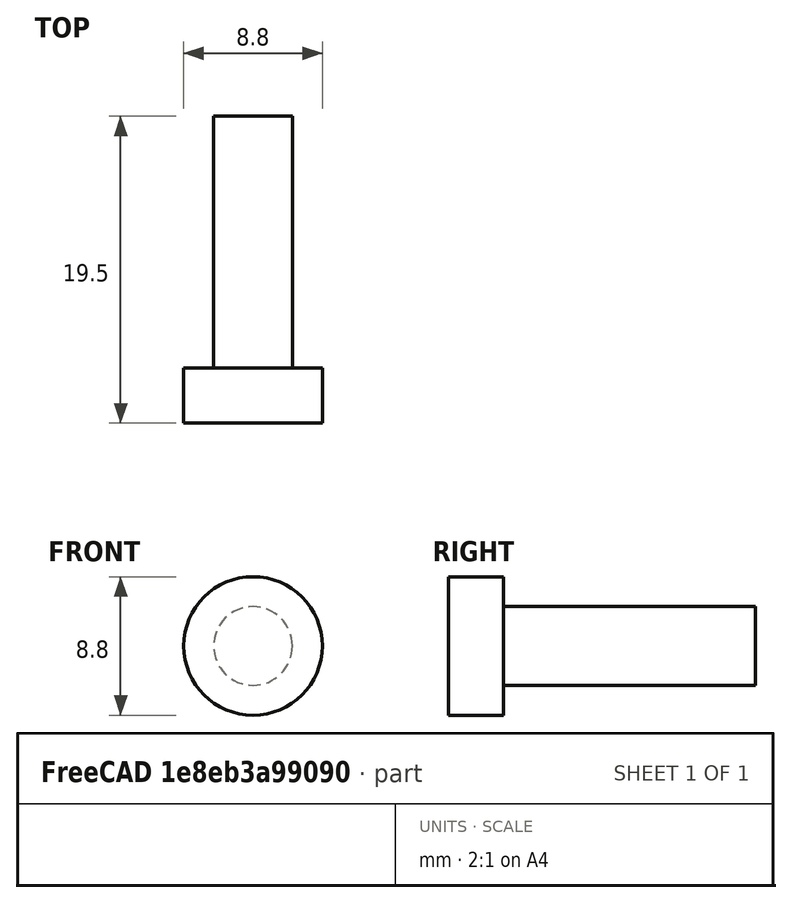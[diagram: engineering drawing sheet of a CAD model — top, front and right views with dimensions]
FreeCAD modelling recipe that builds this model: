
FCSTD DOCUMENT  (FreeCAD 1.0R39319 (Git))
Label: visM5L16
License: All rights reserved
LicenseURL: https://en.wikipedia.org/wiki/All_rights_reserved
objects: Sketcher::SketchObject×1, PartDesign::Revolution×1, PartDesign::Body×1
note: 6 computed .brp shape members not serialized (recipe doc carries the construction recipe); baked Part::Feature solids carry a one-line shape summary decoded from their .brp

FEATURE [Sketcher::SketchObject] Sketch
  ArcFitTolerance = 1e-06
  AttachmentSupport = -> [YZ_Plane]
  FullyConstrained = true
  MakeInternals = false
  MapMode = 5
  Placement = pos=(0,0,0) rot=(0.57735,0.57735,0.57735;2.0944rad)
  sketch-geometry (6):
    g0: LineSegment StartX=-3.5 StartY=0 StartZ=0 EndX=-3.5 EndY=4.4 EndZ=0
    g1: LineSegment StartX=-3.5 StartY=4.4 StartZ=0 EndX=0 EndY=4.4 EndZ=0
    g2: LineSegment StartX=0 StartY=4.4 StartZ=0 EndX=0 EndY=2.5 EndZ=0
    g3: LineSegment StartX=0 StartY=2.5 StartZ=0 EndX=16 EndY=2.5 EndZ=0
    g4: LineSegment StartX=16 StartY=0 StartZ=0 EndX=16 EndY=2.5 EndZ=0
    g5: LineSegment StartX=-3.5 StartY=0 StartZ=0 EndX=16 EndY=0 EndZ=0
  constraints (18):
    c: PointOnObject(g0,g-1)
    c: Vertical(g0)
    c: Coincident(g1,g0)
    c: PointOnObject(g1,g-2)
    c: Horizontal(g1)
    c: Coincident(g2,g1)
    c: PointOnObject(g2,g-2)
    c: Coincident(g3,g2)
    c: Horizontal(g3)
    c: PointOnObject(g4,g-1)
    c: Coincident(g5,g0)
    c: Coincident(g5,g4)
    c: Coincident(g4,g3)
    c: Perpendicular(g-1,g4)
    c: DistanceY(g0,g0) = 4.4
    c: DistanceX(g1,g1) = 3.5
    c: DistanceX(g3,g3) = 16
    c: DistanceY(g4,g4) = 2.5
FEATURE [PartDesign::Revolution] Revolution
  Angle = 360
  Angle2 = 60
  Axis = (1e-16,1,-1e-16)
  Base = (0,0,0)
  Placement = pos=(0,0,0) rot=(1,1,1;2.0944rad)
  Profile = -> Sketch
  ReferenceAxis = -> Y_Axis
  Refine = true
  Suppressed = false
  Type = 0
FEATURE [PartDesign::Body] Body  label="Corps"
  AllowCompound = false
  Group = -> [Sketch,Revolution]
  Origin = -> Origin
  Tip = -> Revolution
